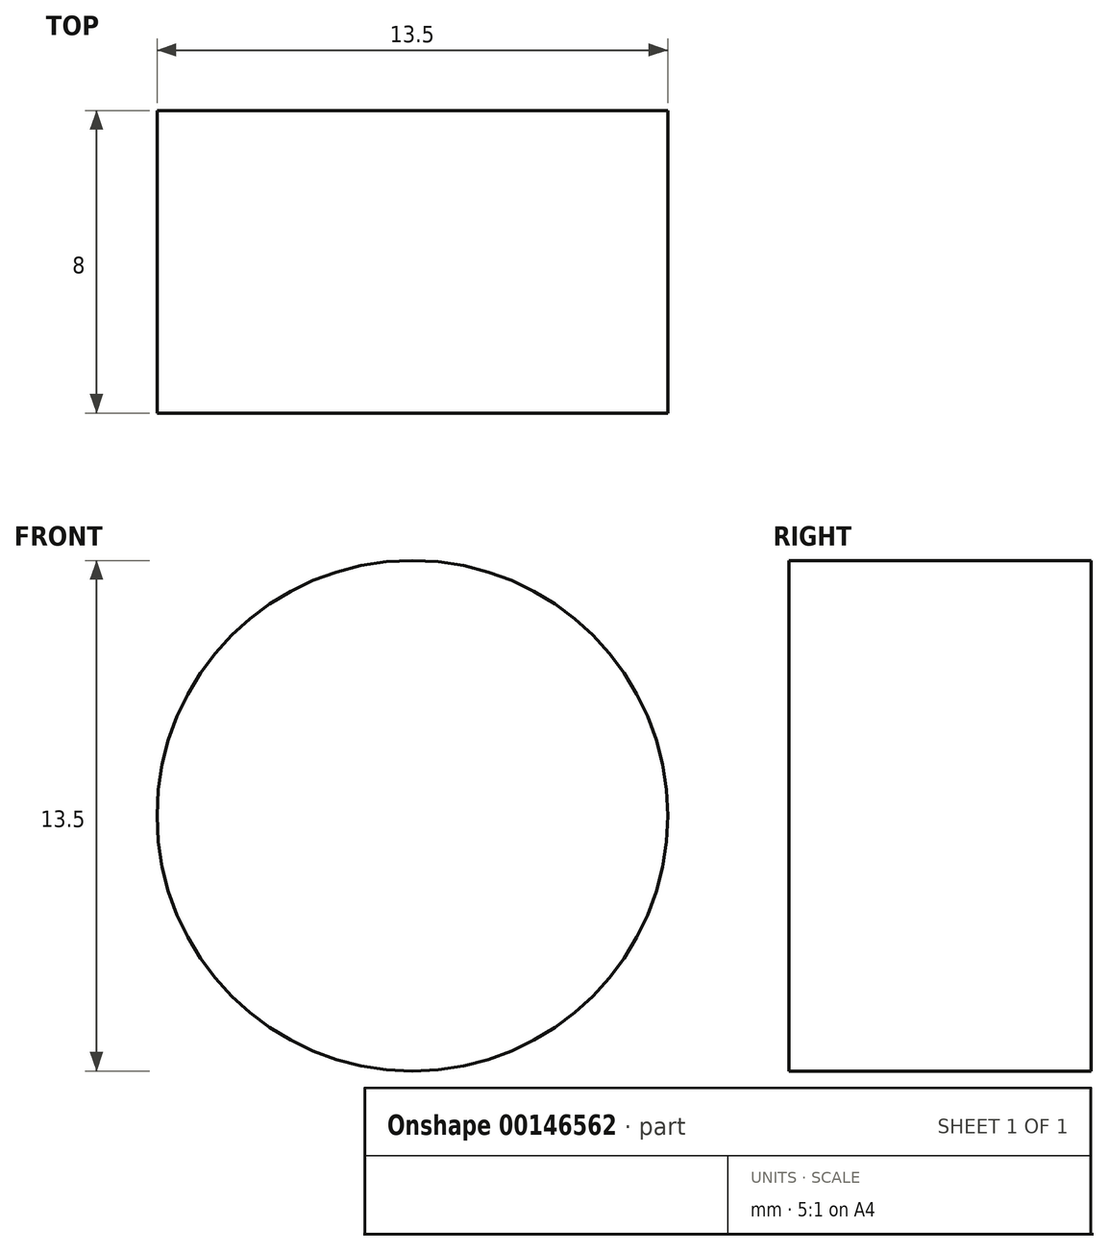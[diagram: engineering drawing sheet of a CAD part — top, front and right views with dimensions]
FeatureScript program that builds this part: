
annotation { "Feature Type Name" : "Feature", "Feature Type Description" : "" }
export const myFeature = defineFeature(function(context is Context, id is Id, definition is map)
    precondition{}
    {
        {
            var Q0;
            Q0=qCreatedBy(makeId("Front.planeOp"),FACE);
            var sketch = newSketch(context, id + "F0", { "sketchPlane" : qUnion([Q0])});
            skCircle(sketch, "E0", {"center": v(0, 0) * mm, "radius": 6.75 * mm});
            skSolve(sketch);
        }
        {
            var Q0;
            Q0 = qSketchRegion(id + "F0", true);
            extrude(context, id + "F1", {"entities" : qUnion([Q0]), "depth" : 8 * mm, "symmetric" : true});
        }
    });
